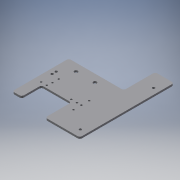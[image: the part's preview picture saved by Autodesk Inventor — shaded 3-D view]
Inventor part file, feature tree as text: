
AUTODESK INVENTOR PART (.ipt)
format: ipt  version: 2016 (Build 200138000, 138)  size: 163,840 bytes
history: native  units: mm
features: reference x15, sketch x5, extrude x4, plane x1, fillet x1
ambient origin geometry x8: Origin, YZ Plane, XZ Plane, XY Plane, X Axis, Y Axis, Z Axis, Center Point
bodies: Solid1 (feature_tree)
feature tree (26):
  plane  "Work Plane1"
  extrude  "Extrusion1"  Depth=6.0mm TaperAngle=0.0deg
  fillet  "Fillet1"  Radius=95.0mm
  sketch  "Sketch2"  dims[d5=63.0mm d6=30.0mm]
  extrude  "Extrusion3"  Depth=30.0mm
  extrude  "Extrusion4"  Depth=300.0mm
  extrude  "Extrusion5"  Depth=100.0mm
  sketch  "Sketch1"  dims[d0=110.0mm d2=6.0mm d3=0.0mm d4=95.0mm]
  sketch  "Sketch3"  dims[d7=180.0mm d10=300.0mm]
  reference  "Reference1"
  reference  "Reference2"
  sketch  "Sketch4"  dims[d11=7.0mm d15=100.0mm]
  reference  "Reference3"
  reference  "Reference4"
  reference  "Reference5"
  reference  "Reference6"
  sketch  "Sketch5"  dims[d17=8.0mm d18=60.0mm d19=60.0mm d27=30.0mm d30=0.0mm d31=0.0mm d32=10.0mm d33=0.0mm d34=0.0mm d35=0.0mm]
  reference  "Reference7"
  reference  "Reference8"
  reference  "Reference9"
  reference  "Reference10"
  reference  "Reference11"
  reference  "Reference12"
  reference  "Reference13"
  reference  "Reference14"
  reference  "Reference15"
